# Revit family: Sanext_Запорный клапан SANEXT LV2, прямой
name_source: partatom
category: Арматура трубопроводов
revit_build: Autodesk Revit 2017 (Build: 20171027_0315(x64)
units: mm (PartAtom-declared; Revit-internal decimal feet)

## family parameters
Всегда вертикально = Да
На основе рабочей плоскости = Нет
Общий = Нет
При загрузке вырезать с полостями = Нет
Размер круглого соединителя = Использовать радиус
Тип детали = Клапан - Вставляется

## types (2) — shared parameters
ADSK_Единица измерения = шт
ADSK_Завод-изготовитель = ООО САНЕКСТ.ПРО
ADSK_Материал наименование = DZR латунь
L1 = 36 мм
L2 = 30 мм
URL = http://sanext.ru
z = 1
Группа модели = Запорный клапан
Изготовитель = ООО САНЕКСТ.ПРО
Материал корпуса = DZR латунь
Рабочее давление = 0.0 кПа
Разработчик = ООО ПРОРУБИМ
Разработчик (телефон) = +7(495)649-85-43
Разработчик модели (URL) = http://prorubim.com
zero-valued in all types: ADSK_Масса

## per-type parameters (varying)
| type | ADSK_Код изделия | ADSK_Наименование | ДиаметрКлапана | Описание | Радиус |
| Ду15 | 6711 | Запорный клапан SANEXT LV2, прямой Ду15 | 15 мм | Запорный клапан SANEXT LV2, прямой Ду15 | 8 мм |
| Ду20 | 6721 | Запорный клапан SANEXT LV2, прямой Ду20 | 20 мм | Запорный клапан SANEXT LV2, прямой Ду20 | 10 мм |
